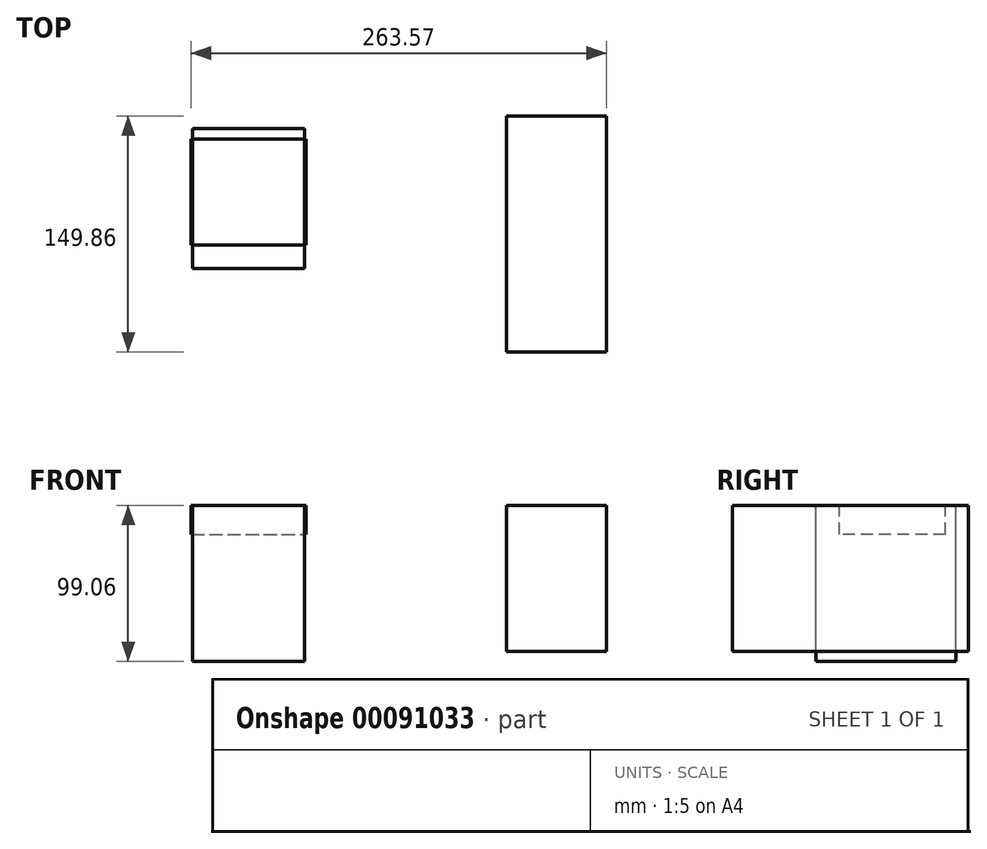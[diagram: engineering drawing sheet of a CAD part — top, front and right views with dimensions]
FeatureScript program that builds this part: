
annotation { "Feature Type Name" : "Feature", "Feature Type Description" : "" }
export const myFeature = defineFeature(function(context is Context, id is Id, definition is map)
    precondition{}
    {
        {
            var Q0;
            Q0=qCreatedBy(makeId("Top.planeOp"),FACE);
            var sketch = newSketch(context, id + "F0", { "sketchPlane" : qUnion([Q0])});
            skLineSegment(sketch, "E0.bottom", {"start": v(-36.45, 29.75) * mm, "end": v(36.45, 29.75) * mm});
            skLineSegment(sketch, "E0.top", {"start": v(-36.45, -37.56) * mm, "end": v(36.45, -37.56) * mm});
            skLineSegment(sketch, "E0.left", {"start": v(-36.45, 29.75) * mm, "end": v(-36.45, -37.56) * mm});
            skLineSegment(sketch, "E0.right", {"start": v(36.45, 29.75) * mm, "end": v(36.45, -37.56) * mm});
            skLineSegment(sketch, "E1", {"start": v(0, 29.75) * mm, "end": v(0, -37.56) * mm, "construction": true});
            skSolve(sketch);
        }
        {
            var Q0;
            Q0 = qSketchRegion(id + "F0", true);
            extrude(context, id + "F1", {"entities" : qUnion([Q0]), "oppositeDirection" : true, "depth" : 18.3 * mm});
        }
        {
            var Q0;
            Q0=qCreatedBy(makeId("Top.planeOp"),FACE);
            var sketch = newSketch(context, id + "F2", { "sketchPlane" : qUnion([Q0])});
            skLineSegment(sketch, "E2.bottom", {"start": v(-35.56, 36.43) * mm, "end": v(35.56, 36.43) * mm});
            skLineSegment(sketch, "E2.top", {"start": v(-35.56, -52.47) * mm, "end": v(35.56, -52.47) * mm});
            skLineSegment(sketch, "E2.left", {"start": v(-35.56, 36.43) * mm, "end": v(-35.56, -52.47) * mm});
            skLineSegment(sketch, "E2.right", {"start": v(35.56, 36.43) * mm, "end": v(35.56, -52.47) * mm});
            skLineSegment(sketch, "E3", {"start": v(0, 36.43) * mm, "end": v(0, -52.47) * mm, "construction": true});
            skSolve(sketch);
        }
        {
            var Q0;
            Q0 = qSketchRegion(id + "F2", true);
            extrude(context, id + "F3", {"entities" : qUnion([Q0]), "oppositeDirection" : true, "depth" : 99.06 * mm});
        }
        {
            var Q0;
            Q0=qCreatedBy(makeId("Top.planeOp"),FACE);
            var sketch = newSketch(context, id + "F4", { "sketchPlane" : qUnion([Q0])});
            skLineSegment(sketch, "E4.bottom", {"start": v(163.62, 44.27) * mm, "end": v(227.12, 44.27) * mm});
            skLineSegment(sketch, "E4.top", {"start": v(163.62, -105.59) * mm, "end": v(227.12, -105.59) * mm});
            skLineSegment(sketch, "E4.left", {"start": v(163.62, 44.27) * mm, "end": v(163.62, -105.59) * mm});
            skLineSegment(sketch, "E4.right", {"start": v(227.12, 44.27) * mm, "end": v(227.12, -105.59) * mm});
            skSolve(sketch);
        }
        {
            var Q0;
            Q0 = qSketchRegion(id + "F4", true);
            extrude(context, id + "F5", {"entities" : qUnion([Q0]), "oppositeDirection" : true, "depth" : 92.7 * mm});
        }
    });
